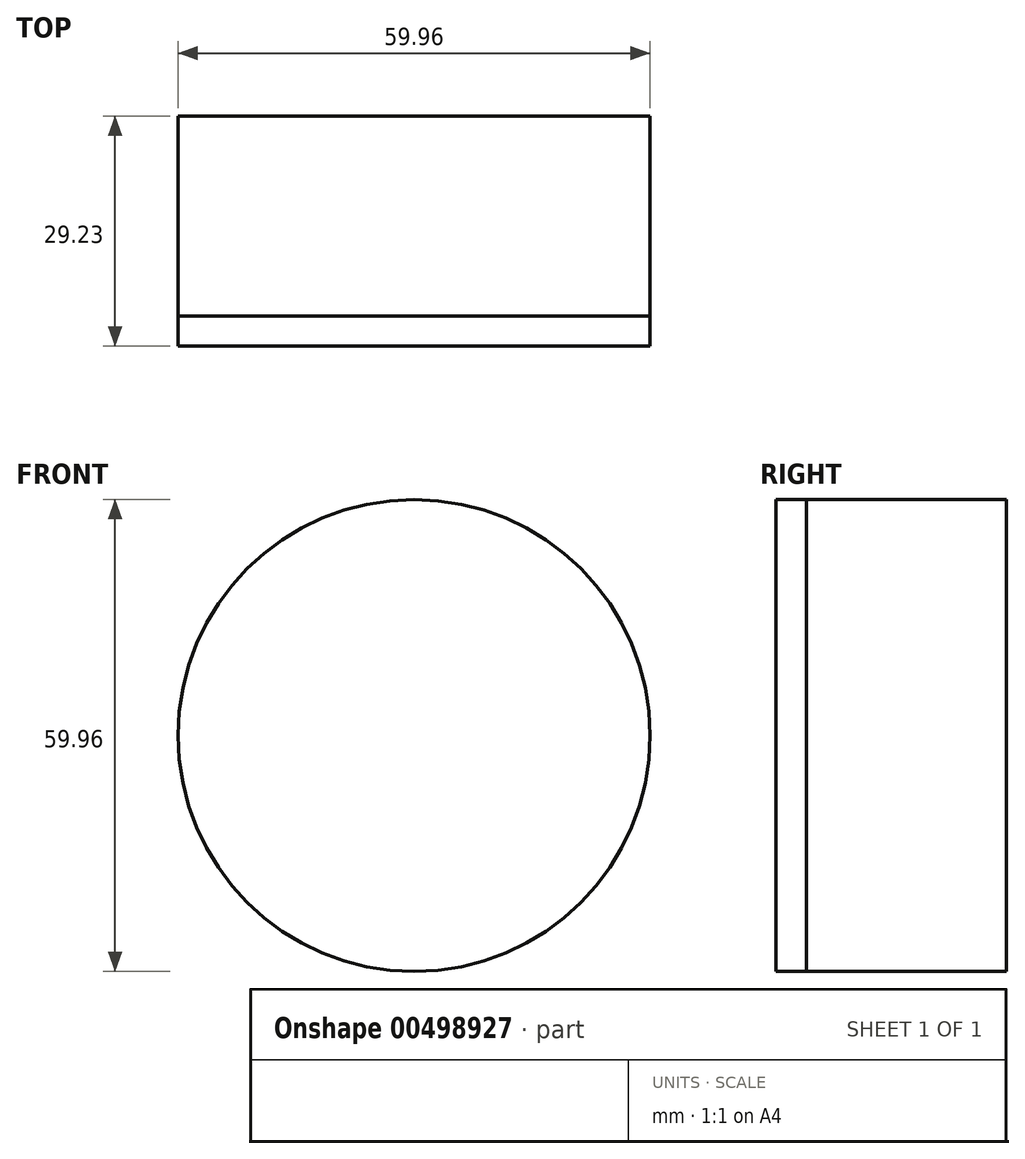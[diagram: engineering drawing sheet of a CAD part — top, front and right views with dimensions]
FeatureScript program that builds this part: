
annotation { "Feature Type Name" : "Feature", "Feature Type Description" : "" }
export const myFeature = defineFeature(function(context is Context, id is Id, definition is map)
    precondition{}
    {
        {
            var Q0;
            Q0=qCreatedBy(makeId("Front.planeOp"),FACE);
            var sketch = newSketch(context, id + "F0", { "sketchPlane" : qUnion([Q0])});
            skCircle(sketch, "E0", {"center": v(0, 0) * mm, "radius": 29.98 * mm});
            skSolve(sketch);
        }
        {
            var Q0;
            Q0=makeQuery(id+"F0.imprint","IMPRINT",FACE,{"disambiguationData":[TD([[makeQuery(id+"F0.imprint","IMPRINT",EDGE,{"derivedFrom":sQuery(id+"F0.wireOp",EDGE,"E0")}),1.0]])]});
            var Q1;
            Q1 = qBodyType(qCreatedBy(id + "F0" ,EDGE), BodyType.WIRE);
            var Q2;
            Q2=sQuery(id+"F0.wireOp",EDGE,"E0");
            extrude(context, id + "F1", {"entities" : qUnion([Q0]), "bodyType" : ToolBodyType.SURFACE, "surfaceEntities" : qUnion([Q1, Q2]), "depth" : 29.23 * mm});
        }
        {
            var Q0;
            Q0 = qBodyType(qCreatedBy(id + "F0" ,EDGE), BodyType.WIRE);
            extrude(context, id + "F2", {"bodyType" : ToolBodyType.SURFACE, "surfaceEntities" : qUnion([Q0]), "depth" : 25.4 * mm});
        }
    });
